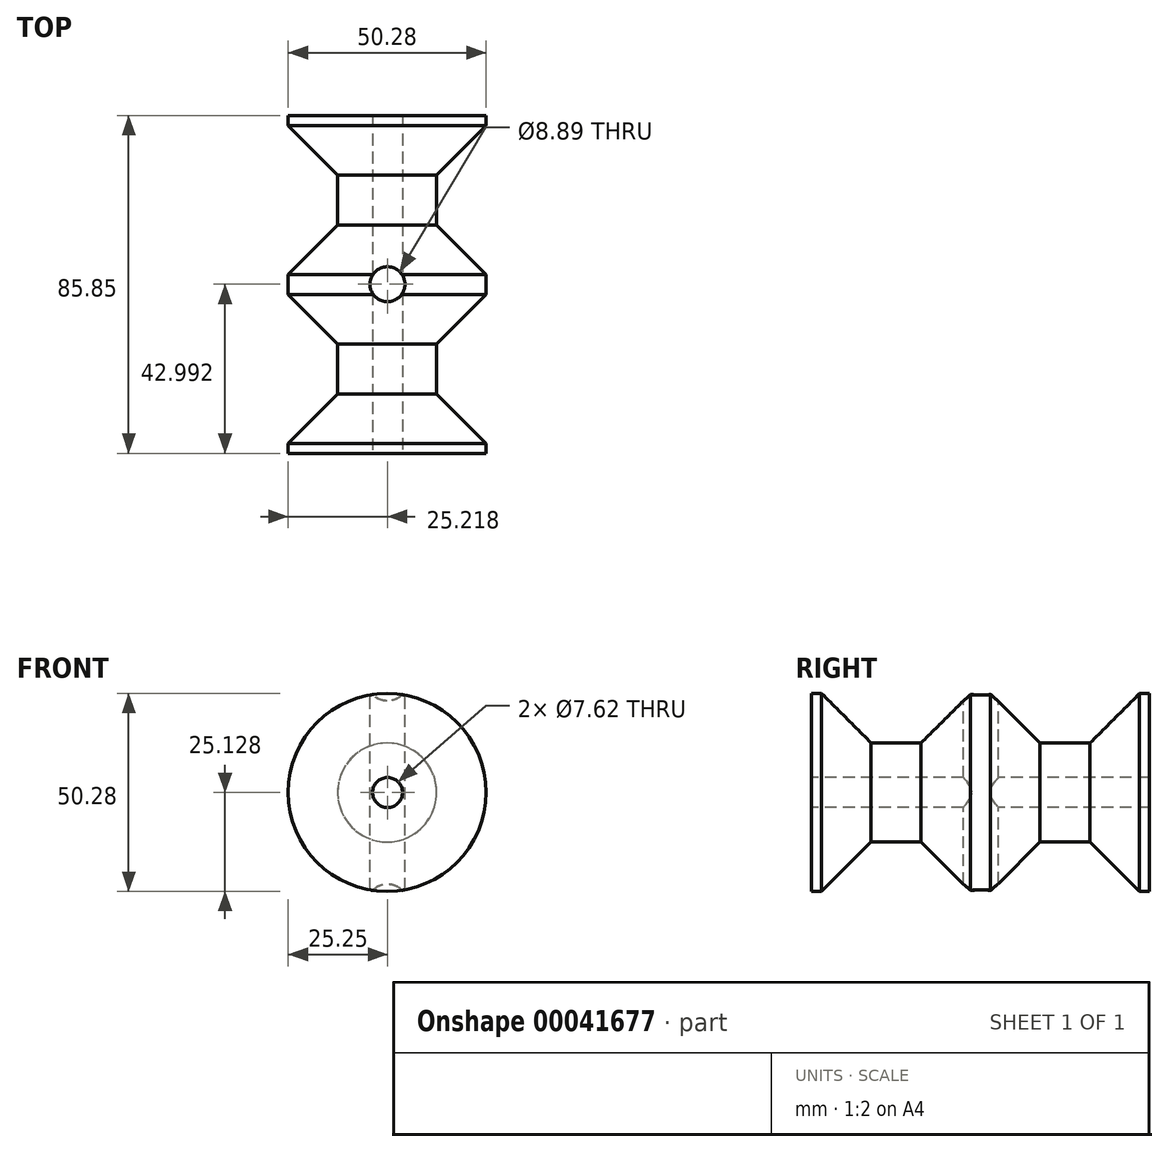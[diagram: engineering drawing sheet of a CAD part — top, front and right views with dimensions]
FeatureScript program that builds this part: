
annotation { "Feature Type Name" : "Feature", "Feature Type Description" : "" }
export const myFeature = defineFeature(function(context is Context, id is Id, definition is map)
    precondition{}
    {
        {
            var Q0;
            Q0=qCreatedBy(makeId("Top.planeOp"),FACE);
            var sketch = newSketch(context, id + "F0", { "sketchPlane" : qUnion([Q0])});
            skLineSegment(sketch, "E0", {"start": v(-25.14, 0) * mm, "end": v(-12.57, 12.57) * mm});
            skLineSegment(sketch, "E1", {"start": v(-12.57, 12.57) * mm, "end": v(-12.57, 25.27) * mm});
            skLineSegment(sketch, "E2", {"start": v(-12.57, 25.27) * mm, "end": v(-25.14, 37.84) * mm});
            skLineSegment(sketch, "E3", {"start": v(-25.14, 37.84) * mm, "end": v(-25.14, 40.38) * mm});
            skLineSegment(sketch, "E4.MirrorCS", {"start": v(-25.14, 42.92) * mm, "end": v(-25.14, 40.38) * mm});
            skLineSegment(sketch, "E5.MirrorCS", {"start": v(-12.57, 55.5) * mm, "end": v(-25.14, 42.92) * mm});
            skLineSegment(sketch, "E6.MirrorCS", {"start": v(-12.57, 68.2) * mm, "end": v(-12.57, 55.5) * mm});
            skLineSegment(sketch, "E7.MirrorCS", {"start": v(-25.14, 80.77) * mm, "end": v(-12.57, 68.2) * mm});
            skLineSegment(sketch, "E8", {"start": v(0, 80.77) * mm, "end": v(0, 0) * mm});
            skLineSegment(sketch, "E9", {"start": v(-25.14, 80.77) * mm, "end": v(-25.14, 83.3) * mm});
            skLineSegment(sketch, "E10", {"start": v(-25.14, 83.3) * mm, "end": v(0, 83.3) * mm});
            skLineSegment(sketch, "E11", {"start": v(0, 83.3) * mm, "end": v(0, 80.77) * mm});
            skLineSegment(sketch, "E12.MirrorCS", {"start": v(-25.14, -2.54) * mm, "end": v(0, -2.54) * mm});
            skLineSegment(sketch, "E13.MirrorCS", {"start": v(0, -2.54) * mm, "end": v(0, 0) * mm});
            skLineSegment(sketch, "E14.MirrorCS", {"start": v(-25.14, 0) * mm, "end": v(-25.14, -2.54) * mm});
            skPoint(sketch, "E15", {"position": v(0, 40.38) * mm});
            skPoint(sketch, "E16", {"position": v(3.5, 83.7) * mm});
            skLineSegment(sketch, "E17", {"start": v(3.58, 83.7) * mm, "end": v(3.58, -11.79) * mm});
            skSolve(sketch);
        }
        {
            var Q0;
            Q0 = qSketchRegion(id + "F0", true);
            var Q1;
            Q1=sQuery(id+"F0.wireOp",EDGE,"E8");
            revolve(context, id + "F1", {"entities" : qUnion([Q0]), "axis" : qUnion([Q1]), "revolveType" : RevolveType.FULL});
        }
        {
            var Q0;
            Q0=qCreatedBy(makeId("Top.planeOp"),FACE);
            cPlane(context, id + "F2", {"entities" : qUnion([Q0]), "cplaneType" : CPlaneType.OFFSET, "offset" : 152.4 * mm, "width" : 152.4 * mm, "height" : 152.4 * mm});
        }
        {
            var Q0;
            Q0=qCreatedBy(id+"F2.planeOp",FACE);
            var sketch = newSketch(context, id + "F3", { "sketchPlane" : qUnion([Q0])});
            skCircle(sketch, "E18", {"center": v(0.08, 40.45) * mm, "radius": 4.45 * mm});
            skSolve(sketch);
        }
        {
            var Q0;
            Q0 = qSketchRegion(id + "F3", true);
            extrude(context, id + "F4", {"entities" : qUnion([Q0]), "operationType" : NewBodyOperationType.REMOVE, "endBound" : BoundingType.THROUGH_ALL, "oppositeDirection" : true, "depth" : 25.4 * mm});
        }
        {
            var Q0;
            Q0=qCreatedBy(makeId("Front.planeOp"),FACE);
            cPlane(context, id + "F5", {"entities" : qUnion([Q0]), "cplaneType" : CPlaneType.OFFSET, "offset" : 152.4 * mm, "width" : 152.4 * mm, "height" : 152.4 * mm});
        }
        {
            var Q0;
            Q0=qCreatedBy(id+"F5.planeOp",FACE);
            var sketch = newSketch(context, id + "F6", { "sketchPlane" : qUnion([Q0])});
            skCircle(sketch, "E19", {"center": v(0.1, -0.01) * mm, "radius": 3.81 * mm});
            skSolve(sketch);
        }
        {
            var Q0;
            Q0 = qSketchRegion(id + "F6", true);
            extrude(context, id + "F7", {"entities" : qUnion([Q0]), "operationType" : NewBodyOperationType.REMOVE, "endBound" : BoundingType.THROUGH_ALL, "oppositeDirection" : true, "depth" : 25.4 * mm});
        }
    });
